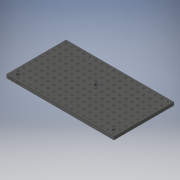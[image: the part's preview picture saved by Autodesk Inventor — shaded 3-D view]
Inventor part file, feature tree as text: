
AUTODESK INVENTOR PART (.ipt)
format: ipt  version: 2019 (Build 230136000, 136)  size: 869,888 bytes
history: mixed  units: in
note: dims shown in document units (in); Inventor stores cm internally (conversion verified against a paired STEP export)
features: extrude x1, sketch x1, projected_geometry x1, other x1, imported_body x1
ambient origin geometry x8: Origin, YZ Plane, XZ Plane, XY Plane, X Axis, Y Axis, Z Axis, Center Point
bodies: Solid1 (imported_parasolid)
feature tree (5):
  extrude  "Extrusion1"  Depth=0.1969in
  sketch  "Sketch1"  dims[d0=0.1969in d1=0.1969in d2=0.1969in d3=0.1969in d4=2.0in d5=0.0in]
  projected_geometry  "Projected Loop1"
  other  "MB1218 - Aluminium Breadboard 304.8 x 457.2 x 12.7mm-1-solid1"
  imported_body  NMx_Import_Brep_tag  [imported B-rep: ~37 faces, bbox_mm=[457.2, 12.7, 254.0]]
